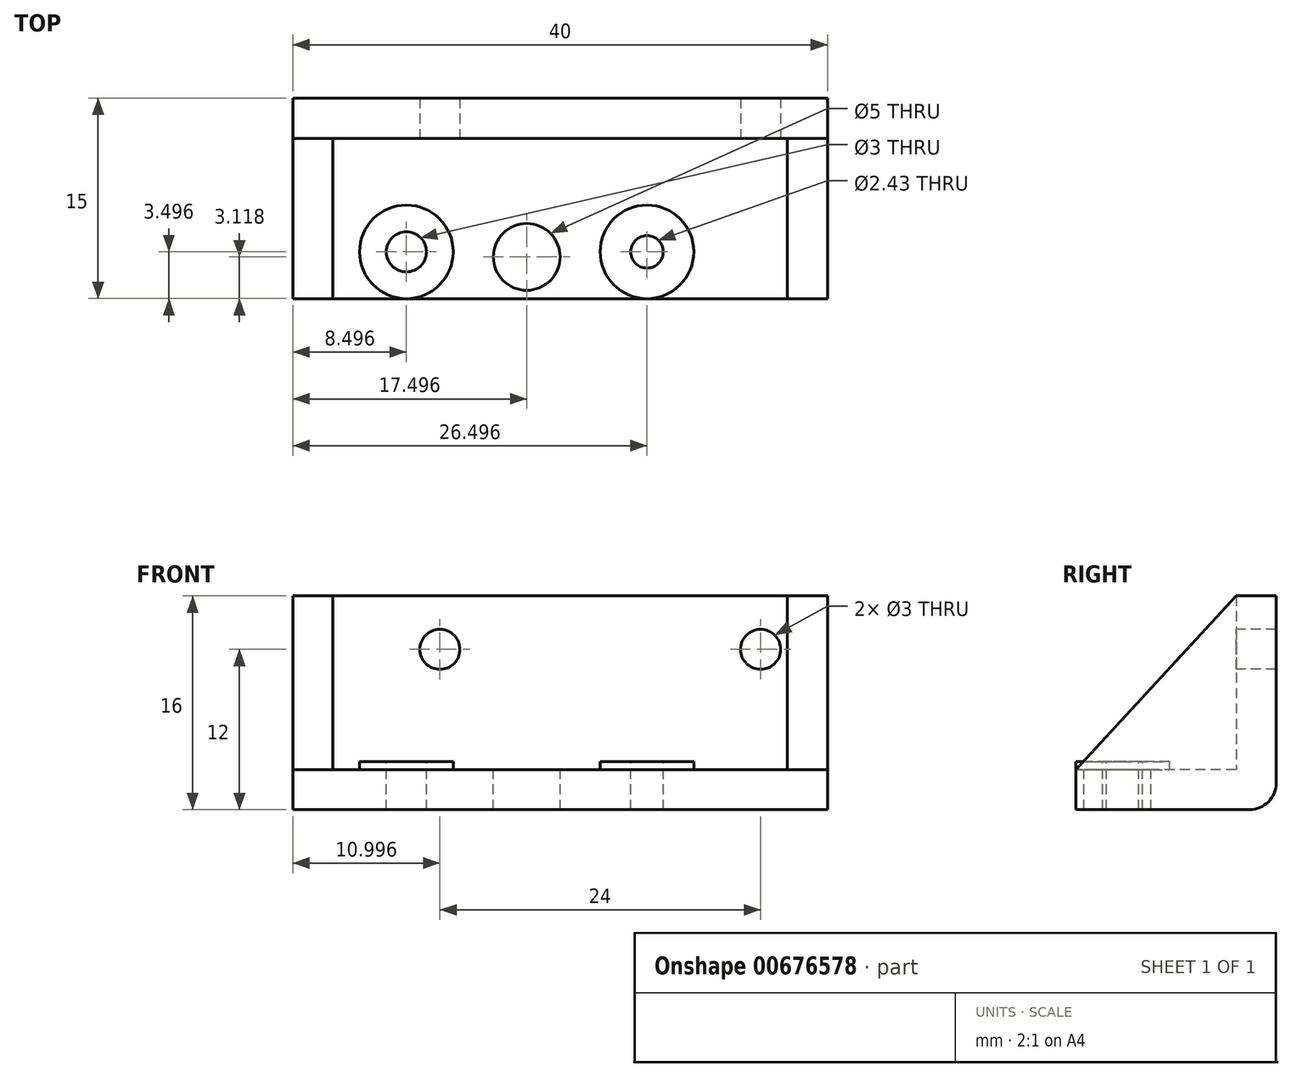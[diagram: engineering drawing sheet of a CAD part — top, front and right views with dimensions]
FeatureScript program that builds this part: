
annotation { "Feature Type Name" : "Feature", "Feature Type Description" : "" }
export const myFeature = defineFeature(function(context is Context, id is Id, definition is map)
    precondition{}
    {
        {
            var Q0;
            Q0=qCreatedBy(makeId("Top.planeOp"),FACE);
            var sketch = newSketch(context, id + "F0", { "sketchPlane" : qUnion([Q0])});
            skLineSegment(sketch, "E0.bottom", {"start": v(-11.94, 6.97) * mm, "end": v(28.06, 6.97) * mm});
            skLineSegment(sketch, "E0.top", {"start": v(-11.94, -8.03) * mm, "end": v(28.06, -8.03) * mm});
            skLineSegment(sketch, "E0.left", {"start": v(-11.94, 6.97) * mm, "end": v(-11.94, -8.03) * mm});
            skLineSegment(sketch, "E0.right", {"start": v(28.06, 6.97) * mm, "end": v(28.06, -8.03) * mm});
            skSolve(sketch);
        }
        {
            var Q0;
            Q0 = qSketchRegion(id + "F0", true);
            extrude(context, id + "F1", {"entities" : qUnion([Q0]), "depth" : 3 * mm, "offsetDistance" : 25 * mm});
        }
        {
            var Q0;
            Q0=makeQuery(id+"F1.opExtrude","CAP_FACE",FACE,{"disambiguationData":[OSD([sQuery(id+"F0.wireOp",EDGE,"E0.bottom"),sQuery(id+"F0.wireOp",EDGE,"E0.top"),sQuery(id+"F0.wireOp",EDGE,"E0.left"),sQuery(id+"F0.wireOp",EDGE,"E0.right")])],"isStart":false});
            var sketch = newSketch(context, id + "F2", { "sketchPlane" : qUnion([Q0])});
            skLineSegment(sketch, "E1", {"start": v(-11.94, 3.97) * mm, "end": v(28.06, 3.97) * mm});
            skLineSegment(sketch, "E2", {"start": v(6.46, 6.97) * mm, "end": v(6.46, 3.97) * mm, "construction": true});
            skSolve(sketch);
        }
        {
            var Q0;
            {var subQ0=sQuery(id+"F2.wireOp",EDGE,"E1");Q0=makeQuery(id+"F2.imprint","IMPRINT",FACE,{"disambiguationData":[TD([[makeQuery(id+"F2.imprint","IMPRINT",EDGE,{"derivedFrom":subQ0}),1.0]])]});}
            extrude(context, id + "F3", {"entities" : qUnion([Q0]), "operationType" : NewBodyOperationType.ADD, "depth" : 13 * mm, "offsetDistance" : 25 * mm});
        }
        {
            var Q0;
            Q0=makeQuery(id+"F3.opExtrude","SWEPT_FACE",FACE,{"disambiguationData":[OSD([sQuery(id+"F2.wireOp",EDGE,"E1")])]});
            var sketch = newSketch(context, id + "F4", { "sketchPlane" : qUnion([Q0])});
            skCircle(sketch, "E3", {"center": v(-0.94, 12) * mm, "radius": 1.5 * mm});
            skCircle(sketch, "E4", {"center": v(23.06, 12) * mm, "radius": 1.5 * mm});
            skLineSegment(sketch, "E5", {"start": v(-0.94, 16) * mm, "end": v(-0.94, 12) * mm, "construction": true});
            skLineSegment(sketch, "E6", {"start": v(23.06, 16) * mm, "end": v(23.06, 12) * mm, "construction": true});
            skLineSegment(sketch, "E7", {"start": v(-0.94, 12) * mm, "end": v(23.06, 12) * mm, "construction": true});
            skSolve(sketch);
        }
        {
            var Q0;
            Q0=makeQuery(id+"F4.imprint","IMPRINT",FACE,{"disambiguationData":[TD([[makeQuery(id+"F4.imprint","IMPRINT",EDGE,{"derivedFrom":sQuery(id+"F4.wireOp",EDGE,"E3")}),1.0]])]});
            var Q1;
            Q1=makeQuery(id+"F4.imprint","IMPRINT",FACE,{"disambiguationData":[TD([[makeQuery(id+"F4.imprint","IMPRINT",EDGE,{"derivedFrom":sQuery(id+"F4.wireOp",EDGE,"E4")}),1.0]])]});
            extrude(context, id + "F5", {"entities" : qUnion([Q0, Q1]), "operationType" : NewBodyOperationType.REMOVE, "oppositeDirection" : true, "depth" : 3 * mm, "offsetDistance" : 25 * mm});
        }
        {
            var Q0;
            Q0=makeQuery(id+"F1.opExtrude","CAP_FACE",FACE,{"disambiguationData":[OSD([sQuery(id+"F0.wireOp",EDGE,"E0.bottom"),sQuery(id+"F0.wireOp",EDGE,"E0.top"),sQuery(id+"F0.wireOp",EDGE,"E0.left"),sQuery(id+"F0.wireOp",EDGE,"E0.right")])],"isStart":false});
            var sketch = newSketch(context, id + "F6", { "sketchPlane" : qUnion([Q0])});
            skCircle(sketch, "E8", {"center": v(5.56, -4.91) * mm, "radius": 2.5 * mm});
            skCircle(sketch, "E9", {"center": v(-3.44, -4.53) * mm, "radius": 1.5 * mm});
            skCircle(sketch, "E10", {"center": v(14.56, -4.53) * mm, "radius": 1.22 * mm});
            skLineSegment(sketch, "E11", {"start": v(14.56, -4.53) * mm, "end": v(14.56, -8.03) * mm});
            skLineSegment(sketch, "E12", {"start": v(-3.44, -4.53) * mm, "end": v(-3.44, -8.03) * mm});
            skCircle(sketch, "E13", {"center": v(14.56, -4.53) * mm, "radius": 3.5 * mm});
            skCircle(sketch, "E14", {"center": v(-3.44, -4.53) * mm, "radius": 3.5 * mm});
            skSolve(sketch);
        }
        {
            var Q0;
            Q0=makeQuery(id+"F6.imprint","IMPRINT",FACE,{"disambiguationData":[TD([[makeQuery(id+"F6.imprint","IMPRINT",EDGE,{"derivedFrom":sQuery(id+"F6.wireOp",EDGE,"E8")}),1.0]])]});
            var Q1;
            Q1=makeQuery(id+"F6.imprint","IMPRINT",FACE,{"disambiguationData":[TD([[makeQuery(id+"F6.imprint","IMPRINT",EDGE,{"derivedFrom":sQuery(id+"F6.wireOp",EDGE,"E9")}),1.0]])]});
            var Q2;
            Q2=makeQuery(id+"F6.imprint","IMPRINT",FACE,{"disambiguationData":[TD([[makeQuery(id+"F6.imprint","IMPRINT",EDGE,{"derivedFrom":sQuery(id+"F6.wireOp",EDGE,"E10")}),1.0]])]});
            extrude(context, id + "F7", {"entities" : qUnion([Q0, Q1, Q2]), "operationType" : NewBodyOperationType.REMOVE, "oppositeDirection" : true, "depth" : 3 * mm, "offsetDistance" : 25 * mm});
        }
        {
            var Q0;
            Q0=makeQuery(id+"F6.imprint","IMPRINT",FACE,{"disambiguationData":[TD([[makeQuery(id+"F6.imprint","IMPRINT",EDGE,{"derivedFrom":sQuery(id+"F6.wireOp",EDGE,"E9")}),-1.0]])]});
            var Q1;
            Q1=makeQuery(id+"F6.imprint","IMPRINT",FACE,{"disambiguationData":[TD([[makeQuery(id+"F6.imprint","IMPRINT",EDGE,{"derivedFrom":sQuery(id+"F6.wireOp",EDGE,"E10")}),-1.0]])]});
            extrude(context, id + "F8", {"entities" : qUnion([Q0, Q1]), "operationType" : NewBodyOperationType.ADD, "depth" : 0.6 * mm, "offsetDistance" : 25 * mm});
        }
        {
            var Q0;
            Q0=makeQuery(id+"F1.opExtrude","CAP_EDGE",EDGE,{"disambiguationData":[OSD([sQuery(id+"F0.wireOp",EDGE,"E0.bottom")])],"isStart":true});
            fillet(context, id + "F9", {"entities" : qUnion([Q0]), "radius" : 2 * mm, "tangentPropagation" : true, "allowEdgeOverflow" : false});
        }
        {
            var Q0;
            {var subQ0=sQuery(id+"F0.wireOp",EDGE,"E0.left");Q0=makeQuery(id+"F3.boolean.opBoolean","MERGE",FACE,{"derivedFrom":[makeQuery(id+"F1.opExtrude","SWEPT_FACE",FACE,{"disambiguationData":[OSD([subQ0])]}),makeQuery(id+"F3.opExtrude","SWEPT_FACE",FACE,{"disambiguationData":[OSD([subQ0])]})]});}
            var sketch = newSketch(context, id + "F10", { "sketchPlane" : qUnion([Q0])});
            skLineSegment(sketch, "E15", {"start": v(8.03, 3) * mm, "end": v(-3.97, 16) * mm});
            skSolve(sketch);
        }
        {
            var Q0;
            Q0=makeQuery(id+"F10.imprint","IMPRINT",FACE,{"disambiguationData":[TD([[makeQuery(id+"F10.imprint","IMPRINT",EDGE,{"derivedFrom":sQuery(id+"F10.wireOp",EDGE,"E15")}),1.0]])]});
            extrude(context, id + "F11", {"entities" : qUnion([Q0]), "oppositeDirection" : true, "depth" : 3 * mm, "offsetDistance" : 25 * mm});
        }
        {
            var Q0;
            {var subQ0=sQuery(id+"F0.wireOp",EDGE,"E0.right");Q0=makeQuery(id+"F3.boolean.opBoolean","MERGE",FACE,{"derivedFrom":[makeQuery(id+"F1.opExtrude","SWEPT_FACE",FACE,{"disambiguationData":[OSD([subQ0])]}),makeQuery(id+"F3.opExtrude","SWEPT_FACE",FACE,{"disambiguationData":[OSD([subQ0])]})]});}
            var sketch = newSketch(context, id + "F12", { "sketchPlane" : qUnion([Q0])});
            skLineSegment(sketch, "E16", {"start": v(3.97, 16) * mm, "end": v(-8.03, 3) * mm});
            skSolve(sketch);
        }
        {
            var Q0;
            Q0=makeQuery(id+"F12.imprint","IMPRINT",FACE,{"disambiguationData":[TD([[makeQuery(id+"F12.imprint","IMPRINT",EDGE,{"derivedFrom":sQuery(id+"F12.wireOp",EDGE,"E16")}),1.0]])]});
            extrude(context, id + "F13", {"entities" : qUnion([Q0]), "operationType" : NewBodyOperationType.ADD, "oppositeDirection" : true, "depth" : 3 * mm, "offsetDistance" : 25 * mm});
        }
        {
            var Q0;
            Q0=makeQuery(id+"F11.opExtrude","SWEPT_BODY",BODY,{"disambiguationData":[OSD([sQuery(id+"F0.wireOp",EDGE,"E0.left"),sQuery(id+"F2.wireOp",EDGE,"E1"),sQuery(id+"F10.wireOp",EDGE,"E15")])]});
            deleteBodies(context, id + "F14", {"entities" : qUnion([Q0])});
        }
        {
            var Q0;
            {var subQ0=sQuery(id+"F0.wireOp",EDGE,"E0.left");Q0=makeQuery(id+"F3.boolean.opBoolean","MERGE",FACE,{"derivedFrom":[makeQuery(id+"F1.opExtrude","SWEPT_FACE",FACE,{"disambiguationData":[OSD([subQ0])]}),makeQuery(id+"F3.opExtrude","SWEPT_FACE",FACE,{"disambiguationData":[OSD([subQ0])]})]});}
            var sketch = newSketch(context, id + "F15", { "sketchPlane" : qUnion([Q0])});
            skLineSegment(sketch, "E17", {"start": v(-3.97, 16) * mm, "end": v(8.03, 3) * mm});
            skSolve(sketch);
        }
        {
            var Q0;
            Q0=makeQuery(id+"F15.imprint","IMPRINT",FACE,{"disambiguationData":[TD([[makeQuery(id+"F15.imprint","IMPRINT",EDGE,{"derivedFrom":sQuery(id+"F15.wireOp",EDGE,"E17")}),-1.0]])]});
            extrude(context, id + "F16", {"entities" : qUnion([Q0]), "oppositeDirection" : true, "depth" : 3 * mm, "offsetDistance" : 25 * mm});
        }
    });
